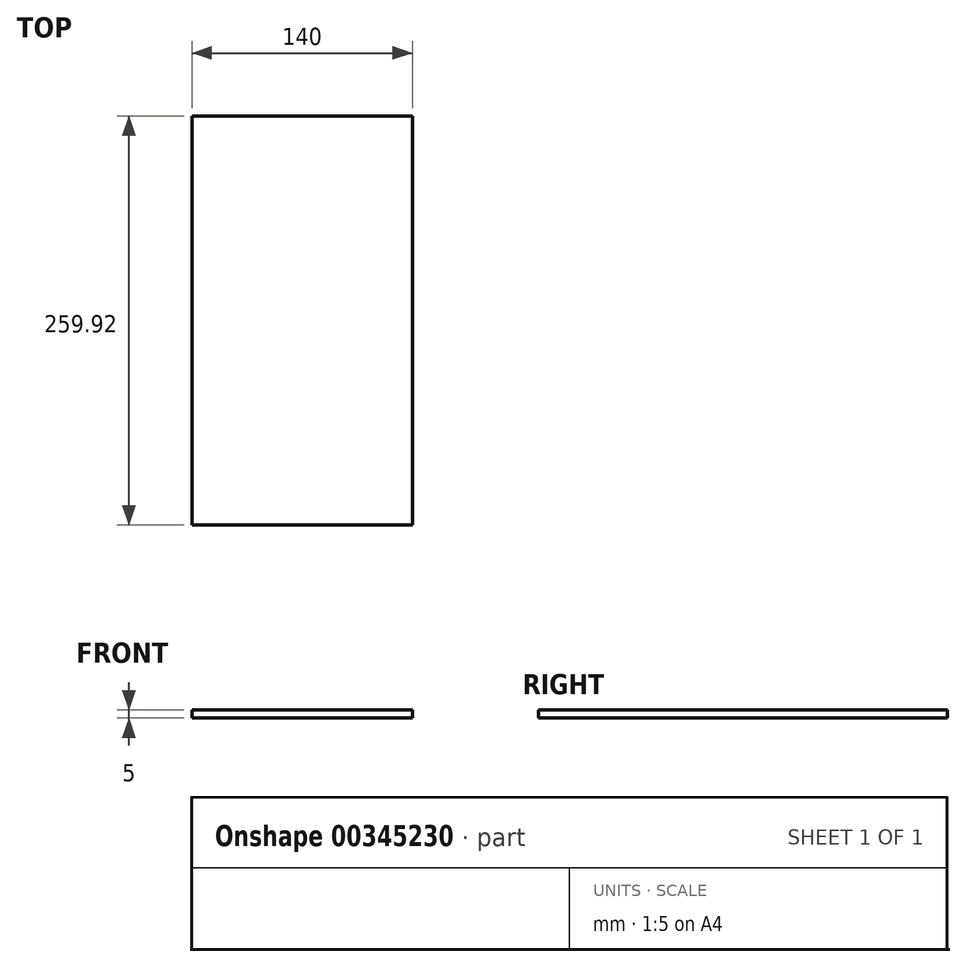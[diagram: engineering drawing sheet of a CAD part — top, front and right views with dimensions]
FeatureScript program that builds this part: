
annotation { "Feature Type Name" : "Feature", "Feature Type Description" : "" }
export const myFeature = defineFeature(function(context is Context, id is Id, definition is map)
    precondition{}
    {
        {
            var Q0;
            Q0=qCreatedBy(makeId("Top.planeOp"),FACE);
            var sketch = newSketch(context, id + "F0", { "sketchPlane" : qUnion([Q0])});
            skLineSegment(sketch, "E0.bottom", {"start": v(-70, 129.96) * mm, "end": v(70, 129.96) * mm});
            skLineSegment(sketch, "E0.top", {"start": v(-70, -129.96) * mm, "end": v(70, -129.96) * mm});
            skLineSegment(sketch, "E0.left", {"start": v(-70, 129.96) * mm, "end": v(-70, -129.96) * mm});
            skLineSegment(sketch, "E0.right", {"start": v(70, 129.96) * mm, "end": v(70, -129.96) * mm});
            skPoint(sketch, "E0.middle", {"position": v(0, 0) * mm});
            skSolve(sketch);
        }
        {
            var Q0;
            Q0=qSketchRegion(id+"F0",true);
            extrude(context, id + "F1", {"entities" : qUnion([Q0]), "depth" : 5 * mm});
        }
    });
